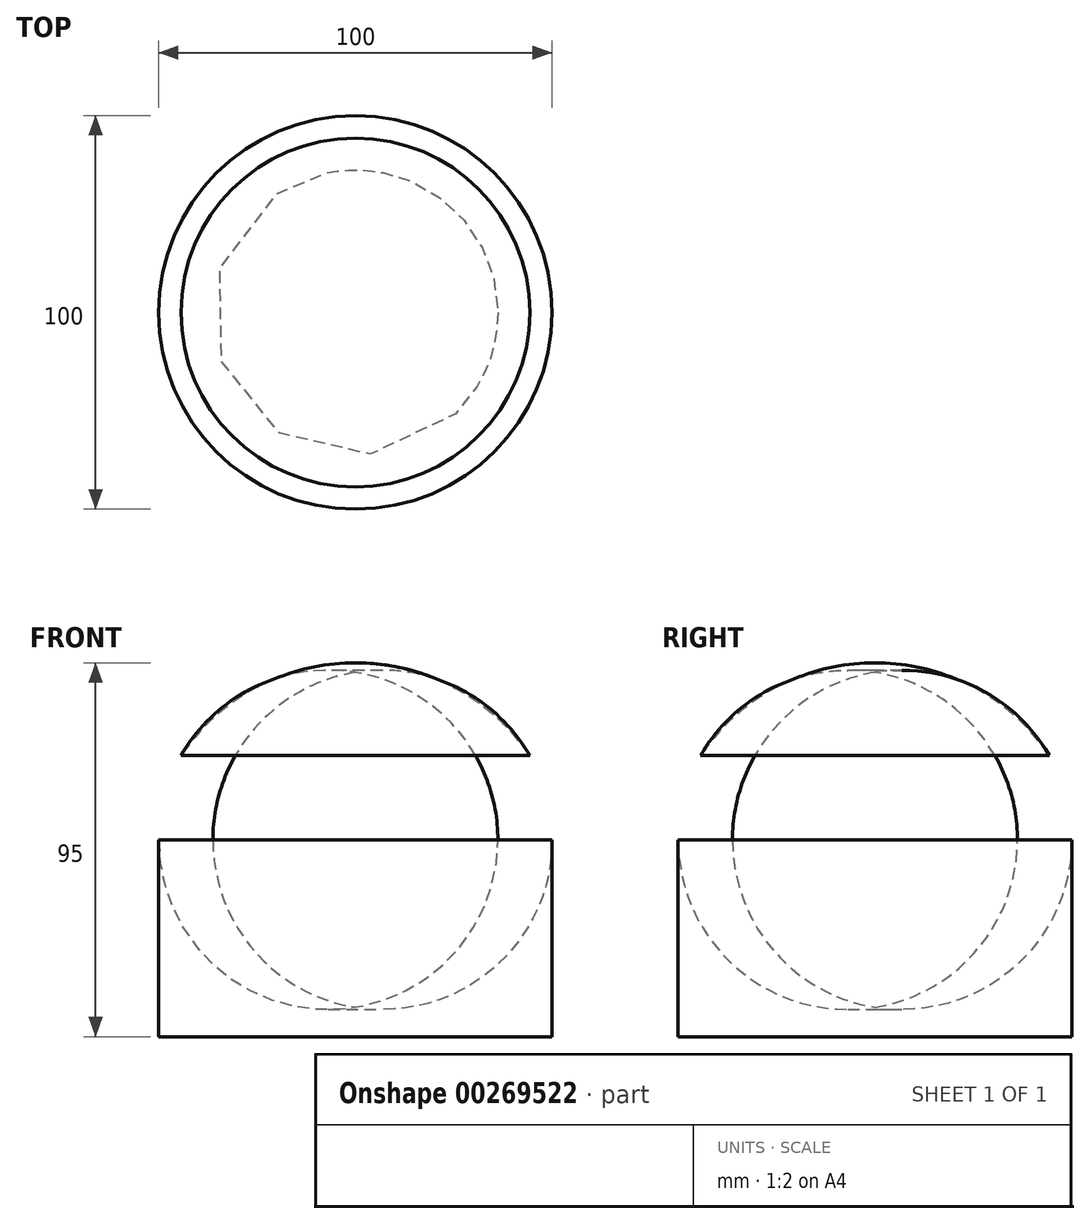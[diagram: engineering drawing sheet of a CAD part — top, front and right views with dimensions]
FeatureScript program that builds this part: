
annotation { "Feature Type Name" : "Feature", "Feature Type Description" : "" }
export const myFeature = defineFeature(function(context is Context, id is Id, definition is map)
    precondition{}
    {
        {
            var Q0;
            Q0=qCreatedBy(makeId("Front.planeOp"),FACE);
            var sketch = newSketch(context, id + "F0", { "sketchPlane" : qUnion([Q0])});
            skLineSegment(sketch, "E0.bottom", {"start": v(0, 0) * mm, "end": v(50, 0) * mm});
            skLineSegment(sketch, "E0.top", {"start": v(0, 50) * mm, "end": v(50, 50) * mm});
            skLineSegment(sketch, "E0.left", {"start": v(0, 0) * mm, "end": v(0, 50) * mm});
            skLineSegment(sketch, "E0.right", {"start": v(50, 0) * mm, "end": v(50, 50) * mm});
            skCircle(sketch, "E1", {"center": v(0, 50) * mm, "radius": 25 * mm, "construction": true});
            skLineSegment(sketch, "E2", {"start": v(0, 50) * mm, "end": v(0, 95) * mm});
            skArc(sketch, "E3", {"start": v(44.31, 71.4) * mm, "mid": v(25.1, 88.73) * mm, "end": v(0, 95) * mm});
            skArc(sketch, "E4", {"start": v(50, 50) * mm, "mid": v(48.55, 61.07) * mm, "end": v(44.31, 71.4) * mm});
            skSolve(sketch);
        }
        {
            var Q0;
            Q0 = qSketchRegion(id + "F0", true);
            var Q1;
            Q1=sQuery(id+"F0.wireOp",EDGE,"E0.left");
            revolve(context, id + "F1", {"entities" : qUnion([Q0]), "axis" : qUnion([Q1]), "revolveType" : RevolveType.FULL});
        }
    });
